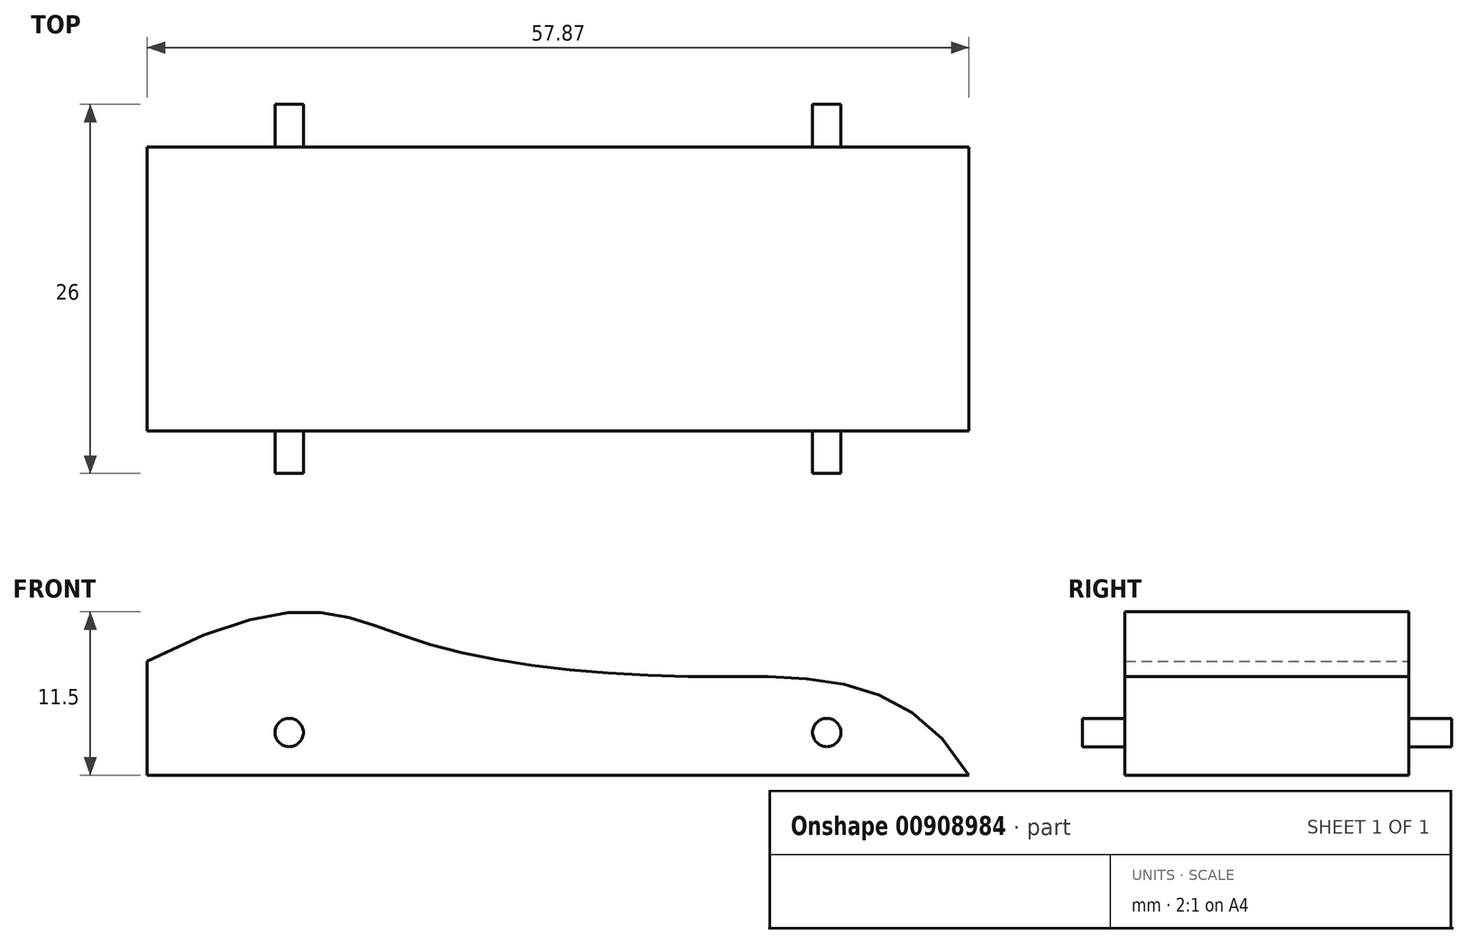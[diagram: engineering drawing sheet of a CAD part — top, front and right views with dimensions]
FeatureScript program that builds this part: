
annotation { "Feature Type Name" : "Feature", "Feature Type Description" : "" }
export const myFeature = defineFeature(function(context is Context, id is Id, definition is map)
    precondition{}
    {
        {
            var Q0;
            Q0=qCreatedBy(makeId("Front.planeOp"),FACE);
            var sketch = newSketch(context, id + "F0", { "sketchPlane" : qUnion([Q0])});
            skLineSegment(sketch, "E0", {"start": v(0, 0) * mm, "end": v(0, 8.02) * mm});
            skLineSegment(sketch, "E1", {"start": v(0, 0) * mm, "end": v(57.87, 0) * mm});
            skFitSpline(sketch, "E2", {"points": [v(57.87, 0) * mm, v(38.72, 6.95) * mm, v(18.93, 9.52) * mm, v(0, 8.02) * mm], "startDerivative": vector(-40.02, 68.08) * mm, "endDerivative": vector(-100.59, -51.54) * mm});
            skSolve(sketch);
        }
        {
            var Q0;
            Q0=makeQuery(id+"F0.imprint","IMPRINT",FACE,{"disambiguationData":[TD([[makeQuery(id+"F0.imprint","IMPRINT",EDGE,{"derivedFrom":sQuery(id+"F0.wireOp",EDGE,"E0")}),-1.0]])]});
            extrude(context, id + "F1", {"entities" : qUnion([Q0]), "depth" : 10 * mm, "offsetDistance" : 25 * mm, "hasSecondDirection" : true, "secondDirectionOppositeDirection" : true, "secondDirectionDepth" : 10 * mm});
        }
        {
            var Q0;
            Q0=makeQuery(id+"F1.opExtrude","CAP_FACE",FACE,{"disambiguationData":[OSD([sQuery(id+"F0.wireOp",EDGE,"E0"),sQuery(id+"F0.wireOp",EDGE,"E1"),sQuery(id+"F0.wireOp",EDGE,"E2")])],"isStart":false});
            var sketch = newSketch(context, id + "F2", { "sketchPlane" : qUnion([Q0])});
            skPoint(sketch, "E3", {"position": v(10, 3) * mm});
            skPoint(sketch, "E4", {"position": v(47.87, 3) * mm});
            skCircle(sketch, "E5", {"center": v(10, 3) * mm, "radius": 1 * mm});
            skCircle(sketch, "E6", {"center": v(47.87, 3) * mm, "radius": 1 * mm});
            skSolve(sketch);
        }
        {
            var Q0;
            Q0 = qSketchRegion(id + "F2", true);
            extrude(context, id + "F3", {"entities" : qUnion([Q0]), "operationType" : NewBodyOperationType.ADD, "depth" : 3 * mm, "offsetDistance" : 25 * mm});
        }
        {
            var Q0;
            Q0=makeQuery(id+"F1.opExtrude","CAP_FACE",FACE,{"disambiguationData":[OSD([sQuery(id+"F0.wireOp",EDGE,"E0"),sQuery(id+"F0.wireOp",EDGE,"E1"),sQuery(id+"F0.wireOp",EDGE,"E2")])],"isStart":true});
            var sketch = newSketch(context, id + "F4", { "sketchPlane" : qUnion([Q0])});
            skCircle(sketch, "E7.0", {"center": v(-47.87, 3) * mm, "radius": 1 * mm});
            skCircle(sketch, "E8.0", {"center": v(-10, 3) * mm, "radius": 1 * mm});
            skSolve(sketch);
        }
        {
            var Q0;
            Q0 = qSketchRegion(id + "F4", true);
            extrude(context, id + "F5", {"entities" : qUnion([Q0]), "operationType" : NewBodyOperationType.ADD, "depth" : 3 * mm, "offsetDistance" : 25 * mm});
        }
    });
